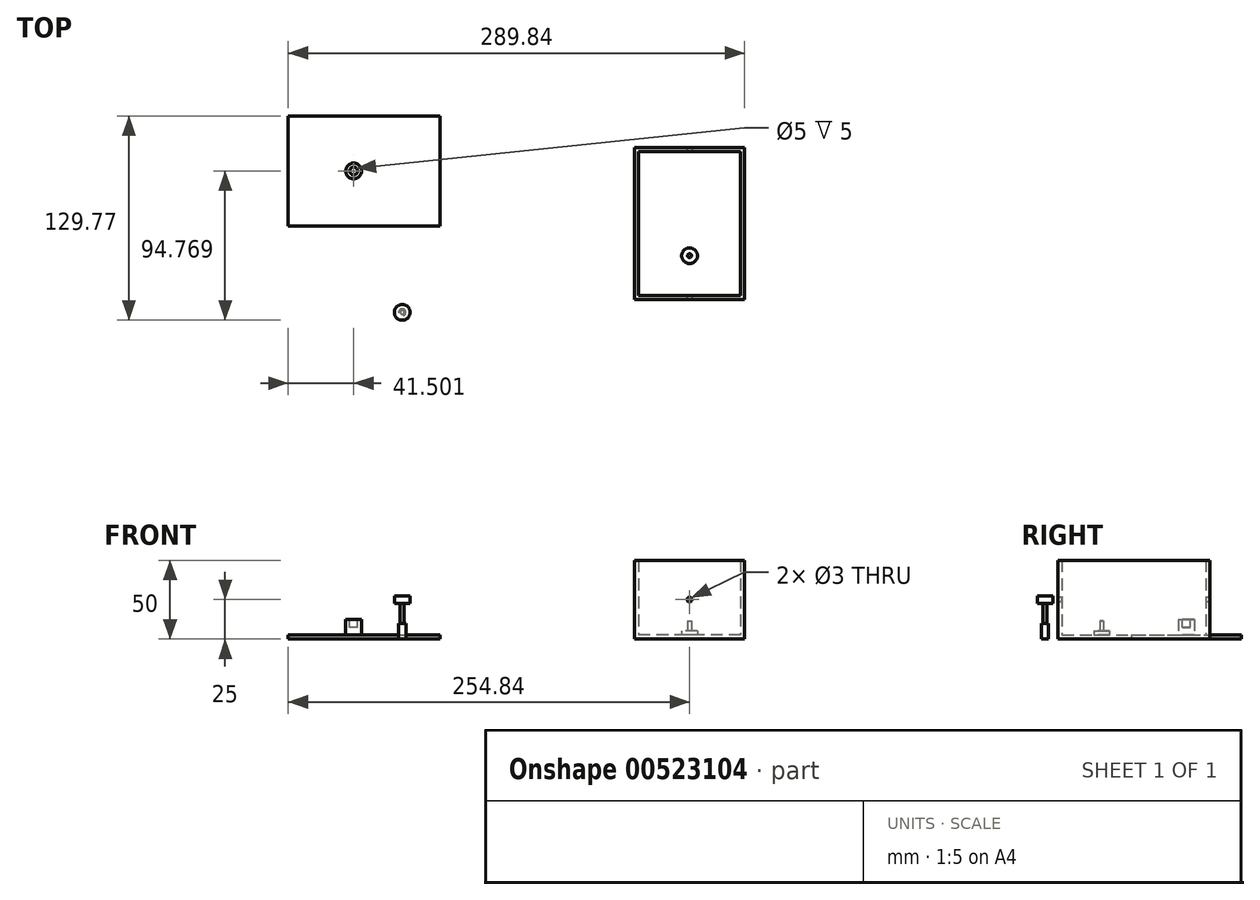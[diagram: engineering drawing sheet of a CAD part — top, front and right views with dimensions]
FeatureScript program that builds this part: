
annotation { "Feature Type Name" : "Feature", "Feature Type Description" : "" }
export const myFeature = defineFeature(function(context is Context, id is Id, definition is map)
    precondition{}
    {
        {
            var Q0;
            Q0=qCreatedBy(makeId("Top.planeOp"),FACE);
            var sketch = newSketch(context, id + "F0", { "sketchPlane" : qUnion([Q0])});
            skLineSegment(sketch, "E0.bottom", {"start": v(35, -32.5) * mm, "end": v(-35, -32.5) * mm});
            skLineSegment(sketch, "E0.left", {"start": v(35, -32.5) * mm, "end": v(35, 32.5) * mm});
            skLineSegment(sketch, "E0.right", {"start": v(-35, -32.5) * mm, "end": v(-35, 32.5) * mm});
            skPoint(sketch, "E0.middle", {"position": v(0, 0) * mm});
            skLineSegment(sketch, "E1.top", {"start": v(-35, 64) * mm, "end": v(35, 64) * mm});
            skLineSegment(sketch, "E1.left", {"start": v(-35, 32.5) * mm, "end": v(-35, 64) * mm});
            skLineSegment(sketch, "E1.right", {"start": v(35, 32.5) * mm, "end": v(35, 64) * mm});
            skSolve(sketch);
        }
        {
            var Q0;
            Q0 = qSketchRegion(id + "F0", true);
            extrude(context, id + "F1", {"entities" : qUnion([Q0]), "depth" : 50 * mm, "offsetDistance" : 25 * mm});
        }
        {
            var Q0;
            Q0=makeQuery(id+"F1.opExtrude","CAP_FACE",FACE,{"disambiguationData":[OSD([sQuery(id+"F0.wireOp",EDGE,"E0.bottom"),sQuery(id+"F0.wireOp",EDGE,"E0.top"),sQuery(id+"F0.wireOp",EDGE,"E0.left"),sQuery(id+"F0.wireOp",EDGE,"E0.right")])],"isStart":false});
            shell(context, id + "F2", {"entities" : qUnion([Q0]), "thickness" : 2.5 * mm});
        }
        {
            var Q0;
            Q0=makeQuery(id+"F1.opExtrude","CAP_FACE",FACE,{"disambiguationData":[OSD([sQuery(id+"F0.wireOp",EDGE,"E0.bottom"),sQuery(id+"F0.wireOp",EDGE,"E0.top"),sQuery(id+"F0.wireOp",EDGE,"E0.left"),sQuery(id+"F0.wireOp",EDGE,"E0.right")])],"isStart":true});
            var sketch = newSketch(context, id + "F3", { "sketchPlane" : qUnion([Q0])});
            skLineSegment(sketch, "E2", {"start": v(0, 0) * mm, "end": v(0, 0) * mm});
            skLineSegment(sketch, "E3", {"start": v(0, 4.75) * mm, "end": v(0, 0) * mm});
            skCircle(sketch, "E4", {"center": v(0, 4.75) * mm, "radius": 1.25 * mm});
            skSolve(sketch);
        }
        {
            var Q0;
            Q0 = qSketchRegion(id + "F3", true);
            extrude(context, id + "F4", {"entities" : qUnion([Q0]), "operationType" : NewBodyOperationType.ADD, "oppositeDirection" : true, "depth" : 11.5 * mm, "offsetDistance" : 25 * mm});
        }
        {
            var Q0;
            Q0=qCreatedBy(makeId("Top.planeOp"),FACE);
            var sketch = newSketch(context, id + "F5", { "sketchPlane" : qUnion([Q0])});
            skLineSegment(sketch, "E5", {"start": v(0, 0) * mm, "end": v(0, 0) * mm});
            skLineSegment(sketch, "E6", {"start": v(0, -4.75) * mm, "end": v(0, 0) * mm});
            skCircle(sketch, "E7", {"center": v(0, -4.75) * mm, "radius": 5 * mm});
            skSolve(sketch);
        }
        {
            var Q0;
            Q0=makeQuery(id+"F5.imprint","IMPRINT",FACE,{"disambiguationData":[TD([[makeQuery(id+"F5.imprint","IMPRINT",EDGE,{"derivedFrom":sQuery(id+"F5.wireOp",EDGE,"E7")}),1.0]])]});
            extrude(context, id + "F6", {"entities" : qUnion([Q0]), "operationType" : NewBodyOperationType.ADD, "depth" : 5 * mm, "offsetDistance" : 25 * mm});
        }
        {
            var Q0;
            Q0=qCreatedBy(makeId("Top.planeOp"),FACE);
            var sketch = newSketch(context, id + "F7", { "sketchPlane" : qUnion([Q0])});
            skLineSegment(sketch, "E8.bottom", {"start": v(-223.34, 14.06) * mm, "end": v(-158.34, 14.06) * mm});
            skLineSegment(sketch, "E8.top", {"start": v(-223.34, 84.06) * mm, "end": v(-158.34, 84.06) * mm});
            skLineSegment(sketch, "E8.left", {"start": v(-223.34, 14.06) * mm, "end": v(-223.34, 84.06) * mm});
            skLineSegment(sketch, "E8.right", {"start": v(-158.34, 14.06) * mm, "end": v(-158.34, 84.06) * mm});
            skPoint(sketch, "E8.middle", {"position": v(-190.84, 49.06) * mm});
            skSolve(sketch);
        }
        {
            var Q0;
            Q0 = qSketchRegion(id + "F7", true);
            extrude(context, id + "F8", {"entities" : qUnion([Q0]), "depth" : 2.5 * mm, "offsetDistance" : 25 * mm});
        }
        {
            var Q0;
            Q0=makeQuery(id+"F8.opExtrude","CAP_FACE",FACE,{"disambiguationData":[OSD([sQuery(id+"F7.wireOp",EDGE,"E8.bottom"),sQuery(id+"F7.wireOp",EDGE,"E8.top"),sQuery(id+"F7.wireOp",EDGE,"E8.left"),sQuery(id+"F7.wireOp",EDGE,"E8.right")])],"isStart":false});
            var sketch = newSketch(context, id + "F9", { "sketchPlane" : qUnion([Q0])});
            skLineSegment(sketch, "E9", {"start": v(-190.84, 14.06) * mm, "end": v(-190.84, 84.06) * mm});
            skLineSegment(sketch, "E10", {"start": v(-190.84, 84.06) * mm, "end": v(-190.84, 49.06) * mm});
            skLineSegment(sketch, "E11", {"start": v(-190.84, 49.06) * mm, "end": v(-213.34, 49.06) * mm});
            skCircle(sketch, "E12", {"center": v(-213.34, 49.06) * mm, "radius": 5 * mm});
            skSolve(sketch);
        }
        {
            var Q0;
            Q0 = qSketchRegion(id + "F9", true);
            extrude(context, id + "F10", {"entities" : qUnion([Q0]), "operationType" : NewBodyOperationType.ADD, "depth" : 10 * mm, "offsetDistance" : 25 * mm});
        }
        {
            var Q0;
            Q0=makeQuery(id+"F10.opExtrude","CAP_FACE",FACE,{"disambiguationData":[OSD([sQuery(id+"F9.wireOp",EDGE,"E12")])],"isStart":false});
            var sketch = newSketch(context, id + "F11", { "sketchPlane" : qUnion([Q0])});
            skCircle(sketch, "E13", {"center": v(-213.34, 49.06) * mm, "radius": 2.5 * mm});
            skSolve(sketch);
        }
        {
            var Q0;
            Q0=makeQuery(id+"F11.imprint","IMPRINT",FACE,{"disambiguationData":[TD([[makeQuery(id+"F11.imprint","IMPRINT",EDGE,{"derivedFrom":sQuery(id+"F11.wireOp",EDGE,"E13")}),1.0]])]});
            var Q1;
            Q1=sQuery(id+"F11.wireOp",EDGE,"E13");
            extrude(context, id + "F12", {"entities" : qUnion([Q0]), "operationType" : NewBodyOperationType.REMOVE, "surfaceEntities" : qUnion([Q1]), "oppositeDirection" : true, "depth" : 5 * mm, "offsetDistance" : 25 * mm});
        }
        {
            var Q0;
            Q0=qCreatedBy(makeId("Top.planeOp"),FACE);
            var sketch = newSketch(context, id + "F13", { "sketchPlane" : qUnion([Q0])});
            skCircle(sketch, "E14", {"center": v(-182.45, -40.7) * mm, "radius": 1.25 * mm});
            skSolve(sketch);
        }
        {
            var Q0;
            Q0 = qSketchRegion(id + "F13", true);
            extrude(context, id + "F14", {"entities" : qUnion([Q0]), "depth" : 22.5 * mm, "offsetDistance" : 25 * mm});
        }
        {
            var Q0;
            Q0=makeQuery(id+"F14.opExtrude","CAP_FACE",FACE,{"disambiguationData":[OSD([sQuery(id+"F13.wireOp",EDGE,"E14")])],"isStart":false});
            var sketch = newSketch(context, id + "F15", { "sketchPlane" : qUnion([Q0])});
            skCircle(sketch, "E15", {"center": v(-182.45, -40.7) * mm, "radius": 5 * mm});
            skSolve(sketch);
        }
        {
            var Q0;
            Q0 = qSketchRegion(id + "F15", true);
            extrude(context, id + "F16", {"entities" : qUnion([Q0]), "operationType" : NewBodyOperationType.ADD, "depth" : 4.8 * mm, "offsetDistance" : 25 * mm});
        }
        {
            var Q0;
            Q0=makeQuery(id+"F8.opExtrude","SWEPT_FACE",FACE,{"disambiguationData":[OSD([sQuery(id+"F7.wireOp",EDGE,"E8.left")])]});
            var sketch = newSketch(context, id + "F17", { "sketchPlane" : qUnion([Q0])});
            skLineSegment(sketch, "E16.bottom", {"start": v(-84.06, 2.5) * mm, "end": v(-14.06, 2.5) * mm});
            skLineSegment(sketch, "E16.top", {"start": v(-84.06, 0) * mm, "end": v(-14.06, 0) * mm});
            skLineSegment(sketch, "E16.left", {"start": v(-84.06, 2.5) * mm, "end": v(-84.06, 0) * mm});
            skLineSegment(sketch, "E16.right", {"start": v(-14.06, 2.5) * mm, "end": v(-14.06, 0) * mm});
            skSolve(sketch);
        }
        {
            var Q0;
            Q0 = qSketchRegion(id + "F17", true);
            extrude(context, id + "F18", {"entities" : qUnion([Q0]), "operationType" : NewBodyOperationType.ADD, "depth" : 31.5 * mm, "offsetDistance" : 25 * mm});
        }
        {
            var Q0;
            {var subQ0=makeQuery(id+"F1.opExtrude","SWEPT_FACE",FACE,{"disambiguationData":[OSD([sQuery(id+"F0.wireOp",EDGE,"E0.bottom")])]});Q0=makeQuery(id+"F6.boolean.opBoolean","MERGE",FACE,{"derivedFrom":[makeQuery(id+"F61JXomXCCskfZS_1.splitOp","SPLIT",FACE,{"derivedFrom":subQ0}),makeQuery(id+"F61JXomXCCskfZS_1.splitOp","SPLIT",FACE,{"derivedFrom":subQ0,"isFromBackBody":true})]});}
            var sketch = newSketch(context, id + "F19", { "sketchPlane" : qUnion([Q0])});
            skLineSegment(sketch, "E17", {"start": v(0, 50) * mm, "end": v(0, 0) * mm});
            skCircle(sketch, "E18", {"center": v(0, 25) * mm, "radius": 1.5 * mm});
            skSolve(sketch);
        }
        {
            var Q0;
            Q0 = qSketchRegion(id + "F19", true);
            extrude(context, id + "F20", {"entities" : qUnion([Q0]), "operationType" : NewBodyOperationType.REMOVE, "oppositeDirection" : true, "depth" : 125 * mm, "offsetDistance" : 25 * mm});
        }
        {
            var Q0;
            Q0=makeQuery(id+"F14.opExtrude","CAP_FACE",FACE,{"disambiguationData":[OSD([sQuery(id+"F13.wireOp",EDGE,"E14")])],"isStart":true});
            var sketch = newSketch(context, id + "F21", { "sketchPlane" : qUnion([Q0])});
            skCircle(sketch, "E19", {"center": v(-182.45, 40.7) * mm, "radius": 2.25 * mm});
            skSolve(sketch);
        }
        {
            var Q0;
            Q0=makeQuery(id+"F21.imprint","IMPRINT",FACE,{"disambiguationData":[TD([[makeQuery(id+"F21.imprint","IMPRINT",EDGE,{"derivedFrom":sQuery(id+"F21.wireOp",EDGE,"E19")}),1.0]])]});
            extrude(context, id + "F22", {"entities" : qUnion([Q0]), "operationType" : NewBodyOperationType.ADD, "oppositeDirection" : true, "depth" : 10 * mm, "offsetDistance" : 25 * mm});
        }
    });
